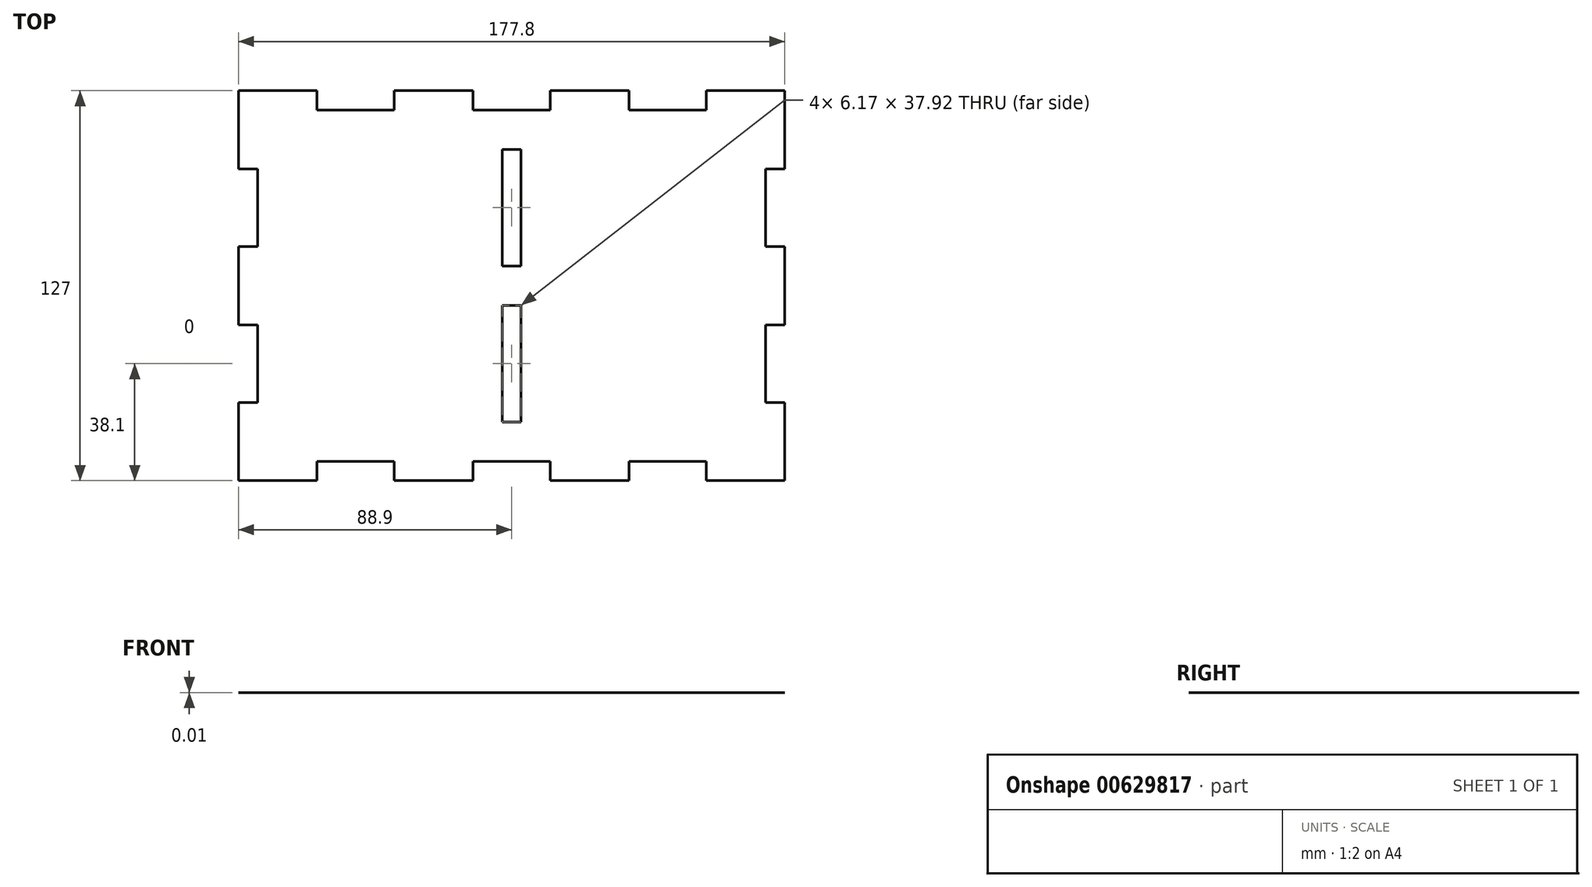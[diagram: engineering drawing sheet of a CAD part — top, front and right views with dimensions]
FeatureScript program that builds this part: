
annotation { "Feature Type Name" : "Feature", "Feature Type Description" : "" }
export const myFeature = defineFeature(function(context is Context, id is Id, definition is map)
    precondition{}
    {
        {
            var Q0;
            Q0=qCreatedBy(makeId("Top.planeOp"),FACE);
            var sketch = newSketch(context, id + "F0", { "sketchPlane" : qUnion([Q0])});
            skLineSegment(sketch, "E0.bottom", {"start": v(0, 0) * mm, "end": v(177.8, 0) * mm});
            skLineSegment(sketch, "E0.top", {"start": v(0, 127) * mm, "end": v(177.8, 127) * mm});
            skLineSegment(sketch, "E0.left", {"start": v(0, 0) * mm, "end": v(0, 127) * mm});
            skLineSegment(sketch, "E0.right", {"start": v(177.8, 0) * mm, "end": v(177.8, 127) * mm});
            skLineSegment(sketch, "E1.bottom", {"start": v(25.49, 0) * mm, "end": v(50.71, 0) * mm});
            skLineSegment(sketch, "E1.top", {"start": v(25.49, 6.26) * mm, "end": v(50.71, 6.26) * mm});
            skLineSegment(sketch, "E1.left", {"start": v(25.49, 0) * mm, "end": v(25.49, 6.26) * mm});
            skLineSegment(sketch, "E1.right", {"start": v(50.71, 0) * mm, "end": v(50.71, 6.26) * mm});
            skPoint(sketch, "E2", {"position": v(38.1, 6.26) * mm});
            skLineSegment(sketch, "E3.bottom", {"start": v(76.29, 0) * mm, "end": v(101.51, 0) * mm});
            skLineSegment(sketch, "E3.top", {"start": v(76.29, 6.26) * mm, "end": v(101.51, 6.26) * mm});
            skLineSegment(sketch, "E3.left", {"start": v(76.29, 0) * mm, "end": v(76.29, 6.26) * mm});
            skLineSegment(sketch, "E3.right", {"start": v(101.51, 0) * mm, "end": v(101.51, 6.26) * mm});
            skPoint(sketch, "E4", {"position": v(88.9, 6.26) * mm});
            skLineSegment(sketch, "E5.bottom", {"start": v(127.09, 6.26) * mm, "end": v(152.31, 6.26) * mm});
            skLineSegment(sketch, "E5.top", {"start": v(127.09, 0) * mm, "end": v(152.31, 0) * mm});
            skLineSegment(sketch, "E5.left", {"start": v(127.09, 6.26) * mm, "end": v(127.09, 0) * mm});
            skLineSegment(sketch, "E5.right", {"start": v(152.31, 6.26) * mm, "end": v(152.31, 0) * mm});
            skPoint(sketch, "E6", {"position": v(139.7, 6.26) * mm});
            skLineSegment(sketch, "E7.bottom", {"start": v(177.8, 50.71) * mm, "end": v(171.54, 50.71) * mm});
            skLineSegment(sketch, "E7.top", {"start": v(177.8, 25.49) * mm, "end": v(171.54, 25.49) * mm});
            skLineSegment(sketch, "E7.left", {"start": v(177.8, 50.71) * mm, "end": v(177.8, 25.49) * mm});
            skLineSegment(sketch, "E7.right", {"start": v(171.54, 50.71) * mm, "end": v(171.54, 25.49) * mm});
            skPoint(sketch, "E8", {"position": v(171.54, 38.1) * mm});
            skLineSegment(sketch, "E9.bottom", {"start": v(177.8, 76.29) * mm, "end": v(171.54, 76.29) * mm});
            skLineSegment(sketch, "E9.top", {"start": v(177.8, 101.51) * mm, "end": v(171.54, 101.51) * mm});
            skLineSegment(sketch, "E9.left", {"start": v(177.8, 76.29) * mm, "end": v(177.8, 101.51) * mm});
            skLineSegment(sketch, "E9.right", {"start": v(171.54, 76.29) * mm, "end": v(171.54, 101.51) * mm});
            skPoint(sketch, "E10", {"position": v(171.54, 88.9) * mm});
            skLineSegment(sketch, "E11", {"start": v(0, 63.5) * mm, "end": v(177.8, 63.5) * mm, "construction": true});
            skLineSegment(sketch, "E12", {"start": v(88.9, 127) * mm, "end": v(88.9, 0) * mm, "construction": true});
            skLineSegment(sketch, "E13.MirrorCS", {"start": v(25.49, 120.74) * mm, "end": v(50.71, 120.74) * mm});
            skLineSegment(sketch, "E14.MirrorCS", {"start": v(25.49, 127) * mm, "end": v(25.49, 120.74) * mm});
            skLineSegment(sketch, "E15.MirrorCS", {"start": v(50.71, 127) * mm, "end": v(50.71, 120.74) * mm});
            skLineSegment(sketch, "E16.MirrorCS", {"start": v(76.29, 127) * mm, "end": v(76.29, 120.74) * mm});
            skLineSegment(sketch, "E17.MirrorCS", {"start": v(76.29, 120.74) * mm, "end": v(101.51, 120.74) * mm});
            skLineSegment(sketch, "E18.MirrorCS", {"start": v(101.51, 127) * mm, "end": v(101.51, 120.74) * mm});
            skLineSegment(sketch, "E19.MirrorCS", {"start": v(127.09, 120.74) * mm, "end": v(152.31, 120.74) * mm});
            skLineSegment(sketch, "E20.MirrorCS", {"start": v(152.31, 120.74) * mm, "end": v(152.31, 127) * mm});
            skLineSegment(sketch, "E21.MirrorCS", {"start": v(127.09, 120.74) * mm, "end": v(127.09, 127) * mm});
            skLineSegment(sketch, "E22.MirrorCS", {"start": v(6.26, 76.29) * mm, "end": v(6.26, 101.51) * mm});
            skLineSegment(sketch, "E23.MirrorCS", {"start": v(0, 101.51) * mm, "end": v(6.26, 101.51) * mm});
            skLineSegment(sketch, "E24.MirrorCS", {"start": v(0, 76.29) * mm, "end": v(6.26, 76.29) * mm});
            skLineSegment(sketch, "E25.MirrorCS", {"start": v(0, 50.71) * mm, "end": v(6.26, 50.71) * mm});
            skLineSegment(sketch, "E26.MirrorCS", {"start": v(6.26, 50.71) * mm, "end": v(6.26, 25.49) * mm});
            skLineSegment(sketch, "E27.MirrorCS", {"start": v(0, 25.49) * mm, "end": v(6.26, 25.49) * mm});
            skSolve(sketch);
        }
        {
            var Q0;
            Q0=makeQuery(id+"F0.imprint","IMPRINT",FACE,{"disambiguationData":[TD([[makeQuery(id+"F0.imprint","IMPRINT",EDGE,{"derivedFrom":sQuery(id+"F0.wireOp",EDGE,"E1.top")}),1.0]])]});
            extrude(context, id + "F1", {"entities" : qUnion([Q0]), "depth" : 1 / 101.6 * mm, "offsetDistance" : 25.4 * mm});
        }
        {
            var Q0;
            Q0=makeQuery(id+"F1.opExtrude","CAP_FACE",FACE,{"disambiguationData":[OSD([sQuery(id+"F0.wireOp",EDGE,"E0.bottom"),sQuery(id+"F0.wireOp",EDGE,"E0.top"),sQuery(id+"F0.wireOp",EDGE,"E0.left"),sQuery(id+"F0.wireOp",EDGE,"E0.right"),sQuery(id+"F0.wireOp",EDGE,"E1.top"),sQuery(id+"F0.wireOp",EDGE,"E1.left"),sQuery(id+"F0.wireOp",EDGE,"E1.right"),sQuery(id+"F0.wireOp",EDGE,"E3.top"),sQuery(id+"F0.wireOp",EDGE,"E3.left"),sQuery(id+"F0.wireOp",EDGE,"E3.right"),sQuery(id+"F0.wireOp",EDGE,"E5.bottom"),sQuery(id+"F0.wireOp",EDGE,"E5.left"),sQuery(id+"F0.wireOp",EDGE,"E5.right"),sQuery(id+"F0.wireOp",EDGE,"E7.bottom"),sQuery(id+"F0.wireOp",EDGE,"E7.top"),sQuery(id+"F0.wireOp",EDGE,"E7.right"),sQuery(id+"F0.wireOp",EDGE,"E9.bottom"),sQuery(id+"F0.wireOp",EDGE,"E9.top"),sQuery(id+"F0.wireOp",EDGE,"E9.right"),sQuery(id+"F0.wireOp",EDGE,"E13.MirrorCS"),sQuery(id+"F0.wireOp",EDGE,"E14.MirrorCS"),sQuery(id+"F0.wireOp",EDGE,"E15.MirrorCS"),sQuery(id+"F0.wireOp",EDGE,"E16.MirrorCS"),sQuery(id+"F0.wireOp",EDGE,"E17.MirrorCS"),sQuery(id+"F0.wireOp",EDGE,"E18.MirrorCS"),sQuery(id+"F0.wireOp",EDGE,"E19.MirrorCS"),sQuery(id+"F0.wireOp",EDGE,"E20.MirrorCS"),sQuery(id+"F0.wireOp",EDGE,"E21.MirrorCS"),sQuery(id+"F0.wireOp",EDGE,"E22.MirrorCS"),sQuery(id+"F0.wireOp",EDGE,"E23.MirrorCS"),sQuery(id+"F0.wireOp",EDGE,"E24.MirrorCS"),sQuery(id+"F0.wireOp",EDGE,"E25.MirrorCS"),sQuery(id+"F0.wireOp",EDGE,"E26.MirrorCS"),sQuery(id+"F0.wireOp",EDGE,"E27.MirrorCS")])],"isStart":false});
            var sketch = newSketch(context, id + "F2", { "sketchPlane" : qUnion([Q0])});
            skLineSegment(sketch, "E28.bottom", {"start": v(85.81, 107.86) * mm, "end": v(91.99, 107.86) * mm});
            skLineSegment(sketch, "E28.top", {"start": v(85.81, 69.94) * mm, "end": v(91.99, 69.94) * mm});
            skLineSegment(sketch, "E28.left", {"start": v(85.81, 107.86) * mm, "end": v(85.81, 69.94) * mm});
            skLineSegment(sketch, "E28.right", {"start": v(91.99, 107.86) * mm, "end": v(91.99, 69.94) * mm});
            skLineSegment(sketch, "E29.bottom", {"start": v(85.81, 57.06) * mm, "end": v(91.99, 57.06) * mm});
            skLineSegment(sketch, "E29.top", {"start": v(85.81, 19.14) * mm, "end": v(91.99, 19.14) * mm});
            skLineSegment(sketch, "E29.left", {"start": v(85.81, 57.06) * mm, "end": v(85.81, 19.14) * mm});
            skLineSegment(sketch, "E29.right", {"start": v(91.99, 57.06) * mm, "end": v(91.99, 19.14) * mm});
            skPoint(sketch, "E30", {"position": v(88.9, 19.14) * mm});
            skPoint(sketch, "E31", {"position": v(91.99, 38.1) * mm});
            skPoint(sketch, "E32", {"position": v(88.9, 69.94) * mm});
            skPoint(sketch, "E33", {"position": v(91.99, 88.9) * mm});
            skPoint(sketch, "E34", {"position": v(88.9, 6.26) * mm});
            skSolve(sketch);
        }
        {
            var Q0;
            Q0=makeQuery(id+"F2.imprint","IMPRINT",FACE,{"disambiguationData":[TD([[makeQuery(id+"F2.imprint","IMPRINT",EDGE,{"derivedFrom":sQuery(id+"F2.wireOp",EDGE,"E28.bottom")}),-1.0]])]});
            var Q1;
            Q1=makeQuery(id+"F2.imprint","IMPRINT",FACE,{"disambiguationData":[TD([[makeQuery(id+"F2.imprint","IMPRINT",EDGE,{"derivedFrom":sQuery(id+"F2.wireOp",EDGE,"E29.bottom")}),-1.0]])]});
            extrude(context, id + "F3", {"entities" : qUnion([Q0, Q1]), "operationType" : NewBodyOperationType.REMOVE, "endBound" : BoundingType.THROUGH_ALL, "oppositeDirection" : true, "depth" : 25.4 * mm, "offsetDistance" : 25.4 * mm});
        }
    });
